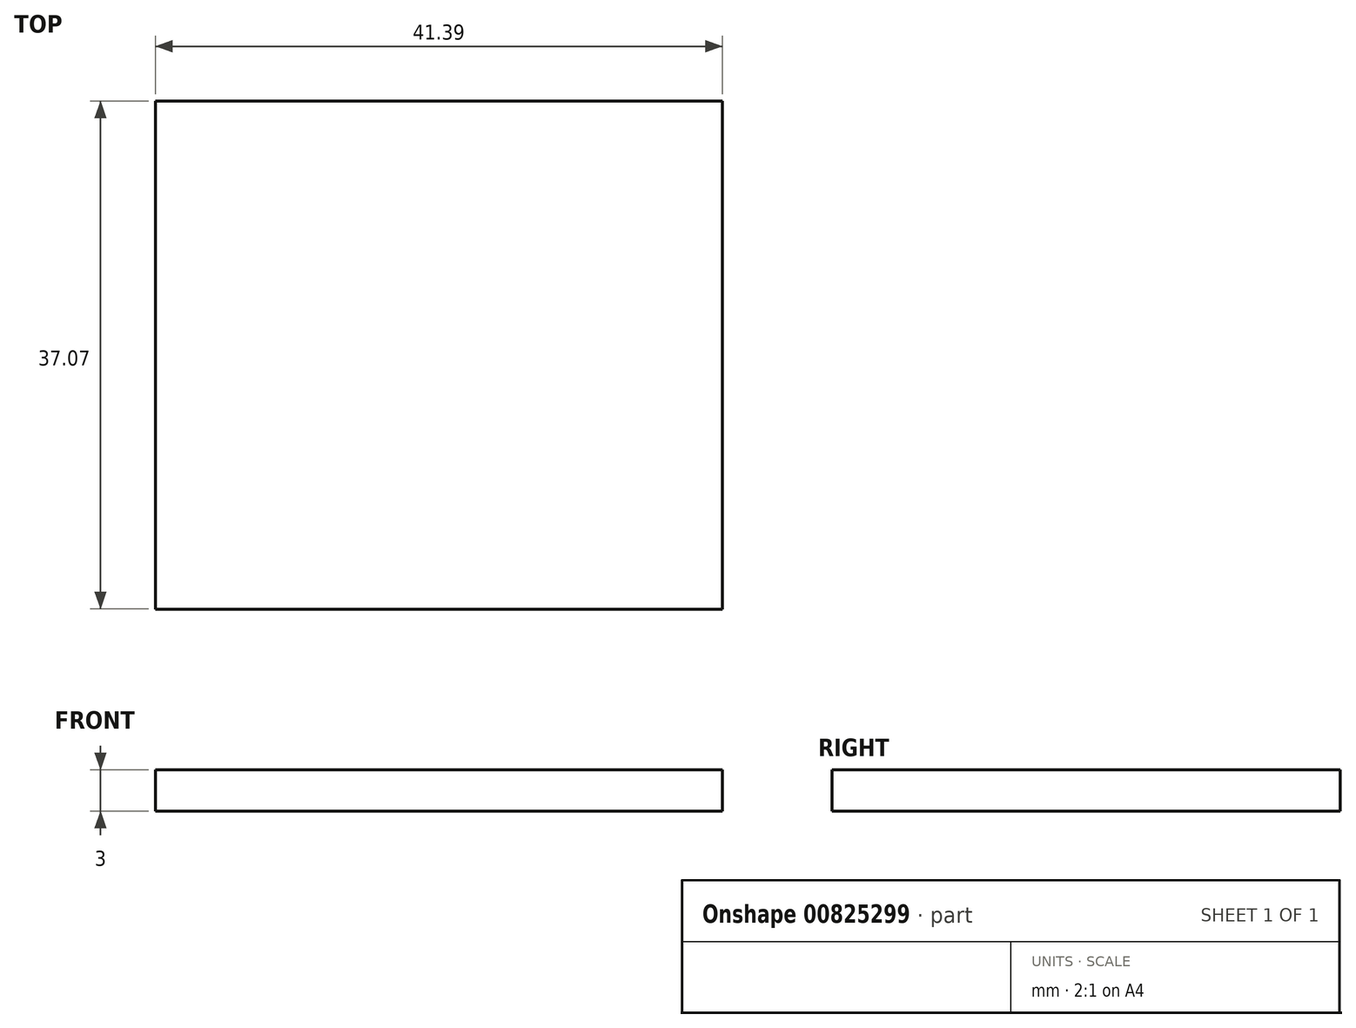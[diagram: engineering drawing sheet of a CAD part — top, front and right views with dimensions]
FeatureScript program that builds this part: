
annotation { "Feature Type Name" : "Feature", "Feature Type Description" : "" }
export const myFeature = defineFeature(function(context is Context, id is Id, definition is map)
    precondition{}
    {
        {
            var Q0;
            Q0=qCreatedBy(makeId("Top.planeOp"),FACE);
            var sketch = newSketch(context, id + "F0", { "sketchPlane" : qUnion([Q0])});
            skLineSegment(sketch, "E0.bottom", {"start": v(-38.08, 50.15) * mm, "end": v(3.3, 50.15) * mm});
            skLineSegment(sketch, "E0.top", {"start": v(-38.08, 13.08) * mm, "end": v(3.3, 13.08) * mm});
            skLineSegment(sketch, "E0.left", {"start": v(-38.08, 50.15) * mm, "end": v(-38.08, 13.08) * mm});
            skLineSegment(sketch, "E0.right", {"start": v(3.3, 50.15) * mm, "end": v(3.3, 13.08) * mm});
            skSolve(sketch);
        }
        {
            var Q0;
            Q0 = qSketchRegion(id + "F0", true);
            extrude(context, id + "F1", {"entities" : qUnion([Q0]), "depth" : 3 * mm, "offsetDistance" : 25 * mm});
        }
    });
